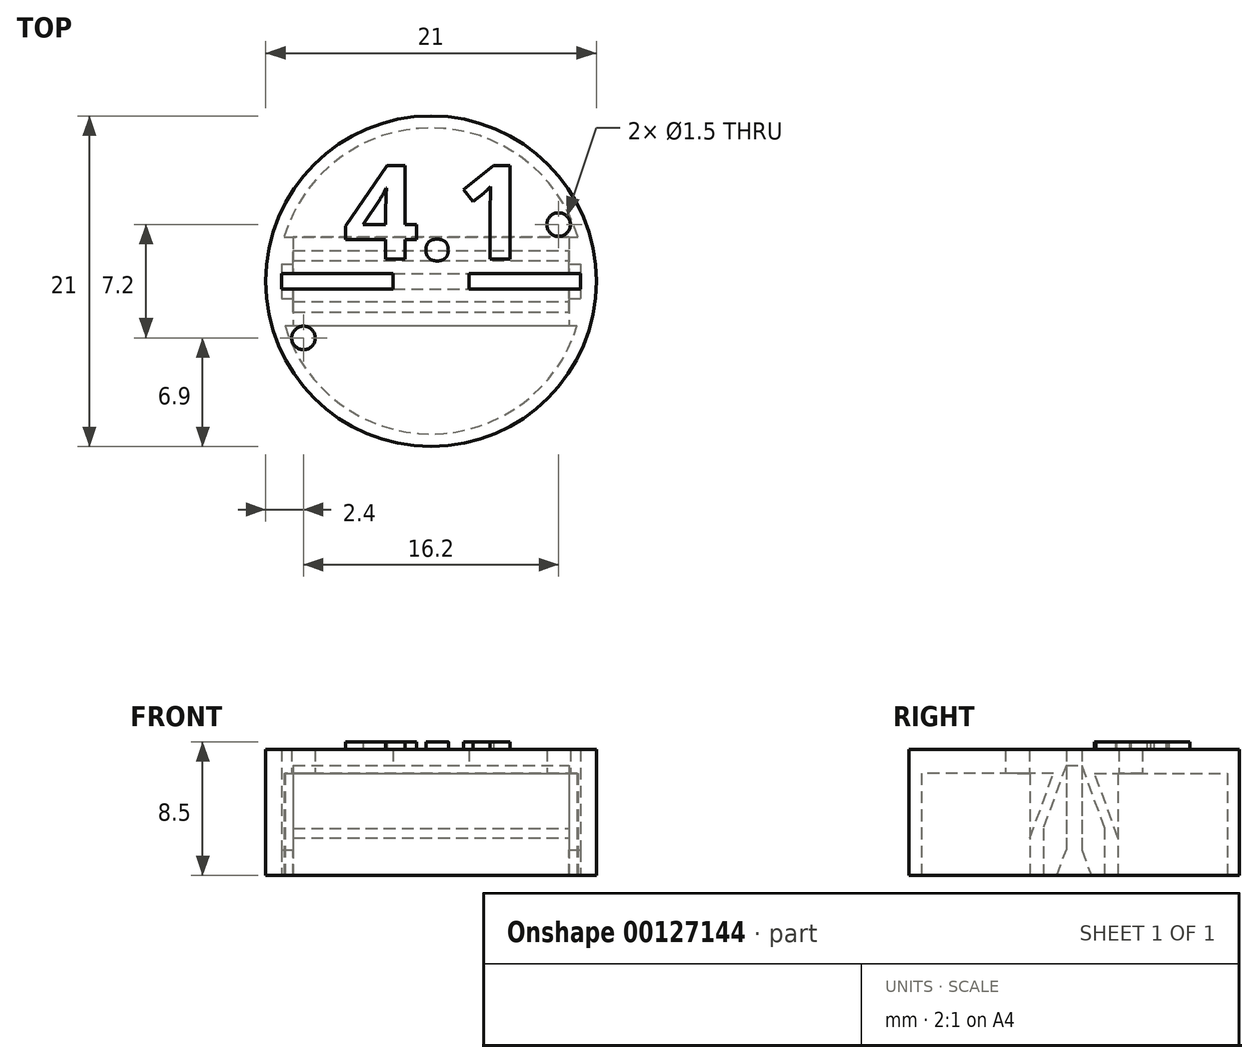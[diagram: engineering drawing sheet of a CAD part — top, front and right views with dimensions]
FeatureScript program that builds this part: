
annotation { "Feature Type Name" : "Feature", "Feature Type Description" : "" }
export const myFeature = defineFeature(function(context is Context, id is Id, definition is map)
    precondition{}
    {
        {
            var Q0;
            Q0=qCreatedBy(makeId("Top.planeOp"),FACE);
            var sketch = newSketch(context, id + "F0", { "sketchPlane" : qUnion([Q0])});
            skCircle(sketch, "E0", {"center": v(0, 0) * mm, "radius": 10.5 * mm});
            skSolve(sketch);
        }
        {
            var Q0;
            Q0=qSketchRegion(id+"F0",true);
            extrude(context, id + "F1", {"entities" : qUnion([Q0]), "oppositeDirection" : true, "depth" : 8 * mm});
        }
        {
            var Q0;
            Q0=makeQuery(id+"F1.opExtrude","CAP_FACE",FACE,{"disambiguationData":[OSD([sQuery(id+"F0.wireOp",EDGE,"E0")])],"isStart":false});
            var sketch = newSketch(context, id + "F2", { "sketchPlane" : qUnion([Q0])});
            skLineSegment(sketch, "E1.bottom", {"start": v(-8.75, 0.5) * mm, "end": v(8.75, 0.5) * mm});
            skLineSegment(sketch, "E1.top", {"start": v(-8.75, -0.5) * mm, "end": v(8.75, -0.5) * mm});
            skLineSegment(sketch, "E1.left", {"start": v(-8.75, 0.5) * mm, "end": v(-8.75, -0.5) * mm});
            skLineSegment(sketch, "E1.right", {"start": v(8.75, 0.5) * mm, "end": v(8.75, -0.5) * mm});
            skPoint(sketch, "E1.middle", {"position": v(0, 0) * mm});
            skSolve(sketch);
        }
        {
            var Q0;
            Q0=qSketchRegion(id+"F2",true);
            extrude(context, id + "F3", {"entities" : qUnion([Q0]), "operationType" : NewBodyOperationType.REMOVE, "oppositeDirection" : true, "depth" : 7 * mm});
        }
        {
            var Q0;
            Q0=makeQuery(id+"F3.boolean.opBoolean","COPY",FACE,{"derivedFrom":makeQuery(id+"F3.opExtrude","SWEPT_FACE",FACE,{"disambiguationData":[OSD([sQuery(id+"F2.wireOp",EDGE,"E1.right")])]})});
            var sketch = newSketch(context, id + "F4", { "sketchPlane" : qUnion([Q0])});
            skLineSegment(sketch, "E2", {"start": v(1.96, -8) * mm, "end": v(-1.96, -8) * mm});
            skLineSegment(sketch, "E3", {"start": v(-1.96, -8) * mm, "end": v(-1.96, -5) * mm});
            skLineSegment(sketch, "E4", {"start": v(-1.96, -5) * mm, "end": v(-0.5, -1) * mm});
            skLineSegment(sketch, "E5", {"start": v(-0.5, -1) * mm, "end": v(0.5, -1) * mm});
            skLineSegment(sketch, "E6", {"start": v(0.5, -1) * mm, "end": v(1.96, -5) * mm});
            skLineSegment(sketch, "E7", {"start": v(1.96, -5) * mm, "end": v(1.96, -8) * mm});
            skLineSegment(sketch, "E8", {"start": v(1.3, -1.5) * mm, "end": v(3, -1.5) * mm});
            skLineSegment(sketch, "E9", {"start": v(3, -1.5) * mm, "end": v(3, -6.17) * mm});
            skLineSegment(sketch, "E10", {"start": v(3, -6.17) * mm, "end": v(1.3, -1.5) * mm});
            skLineSegment(sketch, "E11", {"start": v(-1.3, -1.5) * mm, "end": v(-3, -1.5) * mm});
            skLineSegment(sketch, "E12", {"start": v(-3, -1.5) * mm, "end": v(-3, -6.17) * mm});
            skLineSegment(sketch, "E13", {"start": v(-3, -6.17) * mm, "end": v(-1.3, -1.5) * mm});
            skSolve(sketch);
        }
        {
            var Q0;
            Q0=qSketchRegion(id+"F4",true);
            extrude(context, id + "F5", {"entities" : qUnion([Q0]), "operationType" : NewBodyOperationType.REMOVE, "depth" : 17.5 * mm});
        }
        {
            var Q0;
            Q0=makeQuery(id+"F1.opExtrude","CAP_FACE",FACE,{"disambiguationData":[OSD([sQuery(id+"F0.wireOp",EDGE,"E0")])],"isStart":false});
            var sketch = newSketch(context, id + "F6", { "sketchPlane" : qUnion([Q0])});
            skLineSegment(sketch, "E14.bottom", {"start": v(-9.5, -0.5) * mm, "end": v(9.5, -0.5) * mm});
            skLineSegment(sketch, "E14.top", {"start": v(-9.5, 0.5) * mm, "end": v(9.5, 0.5) * mm});
            skLineSegment(sketch, "E14.left", {"start": v(-9.5, -0.5) * mm, "end": v(-9.5, 0.5) * mm});
            skLineSegment(sketch, "E14.right", {"start": v(9.5, -0.5) * mm, "end": v(9.5, 0.5) * mm});
            skPoint(sketch, "E14.middle", {"position": v(0, 0) * mm});
            skSolve(sketch);
        }
        {
            var Q0;
            Q0=qSketchRegion(id+"F6",true);
            extrude(context, id + "F7", {"entities" : qUnion([Q0]), "operationType" : NewBodyOperationType.REMOVE, "oppositeDirection" : true, "depth" : 7 * mm});
        }
        {
            var Q0;
            Q0=makeQuery(id+"F7.boolean.opBoolean","COPY",FACE,{"derivedFrom":makeQuery(id+"F7.opExtrude","SWEPT_FACE",FACE,{"disambiguationData":[OSD([sQuery(id+"F6.wireOp",EDGE,"E14.right")])]})});
            var sketch = newSketch(context, id + "F8", { "sketchPlane" : qUnion([Q0])});
            skLineSegment(sketch, "E15", {"start": v(0, -5) * mm, "end": v(1.1, -8) * mm});
            skLineSegment(sketch, "E16", {"start": v(1.1, -8) * mm, "end": v(-1.1, -8) * mm});
            skLineSegment(sketch, "E17", {"start": v(-1.1, -8) * mm, "end": v(0, -5) * mm});
            skSolve(sketch);
        }
        {
            var Q0;
            Q0=qSketchRegion(id+"F8",true);
            extrude(context, id + "F9", {"entities" : qUnion([Q0]), "operationType" : NewBodyOperationType.REMOVE, "depth" : 19 * mm});
        }
        {
            var Q0;
            Q0=makeQuery(id+"F1.opExtrude","CAP_FACE",FACE,{"disambiguationData":[OSD([sQuery(id+"F0.wireOp",EDGE,"E0")])],"isStart":false});
            var sketch = newSketch(context, id + "F10", { "sketchPlane" : qUnion([Q0])});
            skLineSegment(sketch, "E18", {"start": v(-9.29, 2.8) * mm, "end": v(9.29, 2.8) * mm});
            skLineSegment(sketch, "E19", {"start": v(-9.33, -2.8) * mm, "end": v(9.33, -2.8) * mm});
            skArc(sketch, "E20", {"start": v(-9.29, 2.8) * mm, "mid": v(0, 9.7) * mm, "end": v(9.29, 2.8) * mm});
            skArc(sketch, "E21", {"start": v(-9.33, -2.8) * mm, "mid": v(0, -9.74) * mm, "end": v(9.33, -2.8) * mm});
            skSolve(sketch);
        }
        {
            var Q0;
            Q0=qSketchRegion(id+"F10",true);
            extrude(context, id + "F11", {"entities" : qUnion([Q0]), "operationType" : NewBodyOperationType.REMOVE, "oppositeDirection" : true, "depth" : 6.5 * mm});
        }
        {
            var Q0;
            Q0=makeQuery(id+"F1.opExtrude","CAP_FACE",FACE,{"disambiguationData":[OSD([sQuery(id+"F0.wireOp",EDGE,"E0")])],"isStart":false});
            var sketch = newSketch(context, id + "F12", { "sketchPlane" : qUnion([Q0])});
            skCircle(sketch, "E22", {"center": v(8.1, -3.6) * mm, "radius": 0.75 * mm});
            skCircle(sketch, "E23", {"center": v(-8.1, 3.6) * mm, "radius": 0.75 * mm});
            skLineSegment(sketch, "E24.bottom", {"start": v(2.4, 0.5) * mm, "end": v(9.5, 0.5) * mm});
            skLineSegment(sketch, "E24.top", {"start": v(2.4, -0.5) * mm, "end": v(9.5, -0.5) * mm});
            skLineSegment(sketch, "E24.left", {"start": v(2.4, 0.5) * mm, "end": v(2.4, -0.5) * mm});
            skLineSegment(sketch, "E24.right", {"start": v(9.5, 0.5) * mm, "end": v(9.5, -0.5) * mm});
            skPoint(sketch, "E24.middle", {"position": v(5.95, 0) * mm});
            skLineSegment(sketch, "E25.bottom", {"start": v(-9.5, 0.5) * mm, "end": v(-2.4, 0.5) * mm});
            skLineSegment(sketch, "E25.top", {"start": v(-9.5, -0.5) * mm, "end": v(-2.4, -0.5) * mm});
            skLineSegment(sketch, "E25.left", {"start": v(-9.5, 0.5) * mm, "end": v(-9.5, -0.5) * mm});
            skLineSegment(sketch, "E25.right", {"start": v(-2.4, 0.5) * mm, "end": v(-2.4, -0.5) * mm});
            skPoint(sketch, "E25.middle", {"position": v(-5.95, 0) * mm});
            skSolve(sketch);
        }
        {
            var Q0;
            Q0=qSketchRegion(id+"F12",true);
            extrude(context, id + "F13", {"entities" : qUnion([Q0]), "operationType" : NewBodyOperationType.REMOVE, "oppositeDirection" : true, "depth" : 8 * mm});
        }
        {
            var Q0;
            Q0=makeQuery(id+"F1.opExtrude","CAP_FACE",FACE,{"disambiguationData":[OSD([sQuery(id+"F0.wireOp",EDGE,"E0")])],"isStart":true});
            var sketch = newSketch(context, id + "F14", { "sketchPlane" : qUnion([Q0])});
            skText(sketch, "E26", { "text": "4.1", "fontName": "OpenSans-Bold.ttf"});
            const initialGuessF14  = {"E26": [-0.00556, 0.0014, 1, 0, 0.006]};
            skSetInitialGuess(sketch, initialGuessF14);
            skSolve(sketch);
        }
        {
            var Q0;
            Q0 = qSketchRegion(id + "F14", true);
            extrude(context, id + "F15", {"entities" : qUnion([Q0]), "operationType" : NewBodyOperationType.ADD, "depth" : 0.5 * mm});
        }
    });
